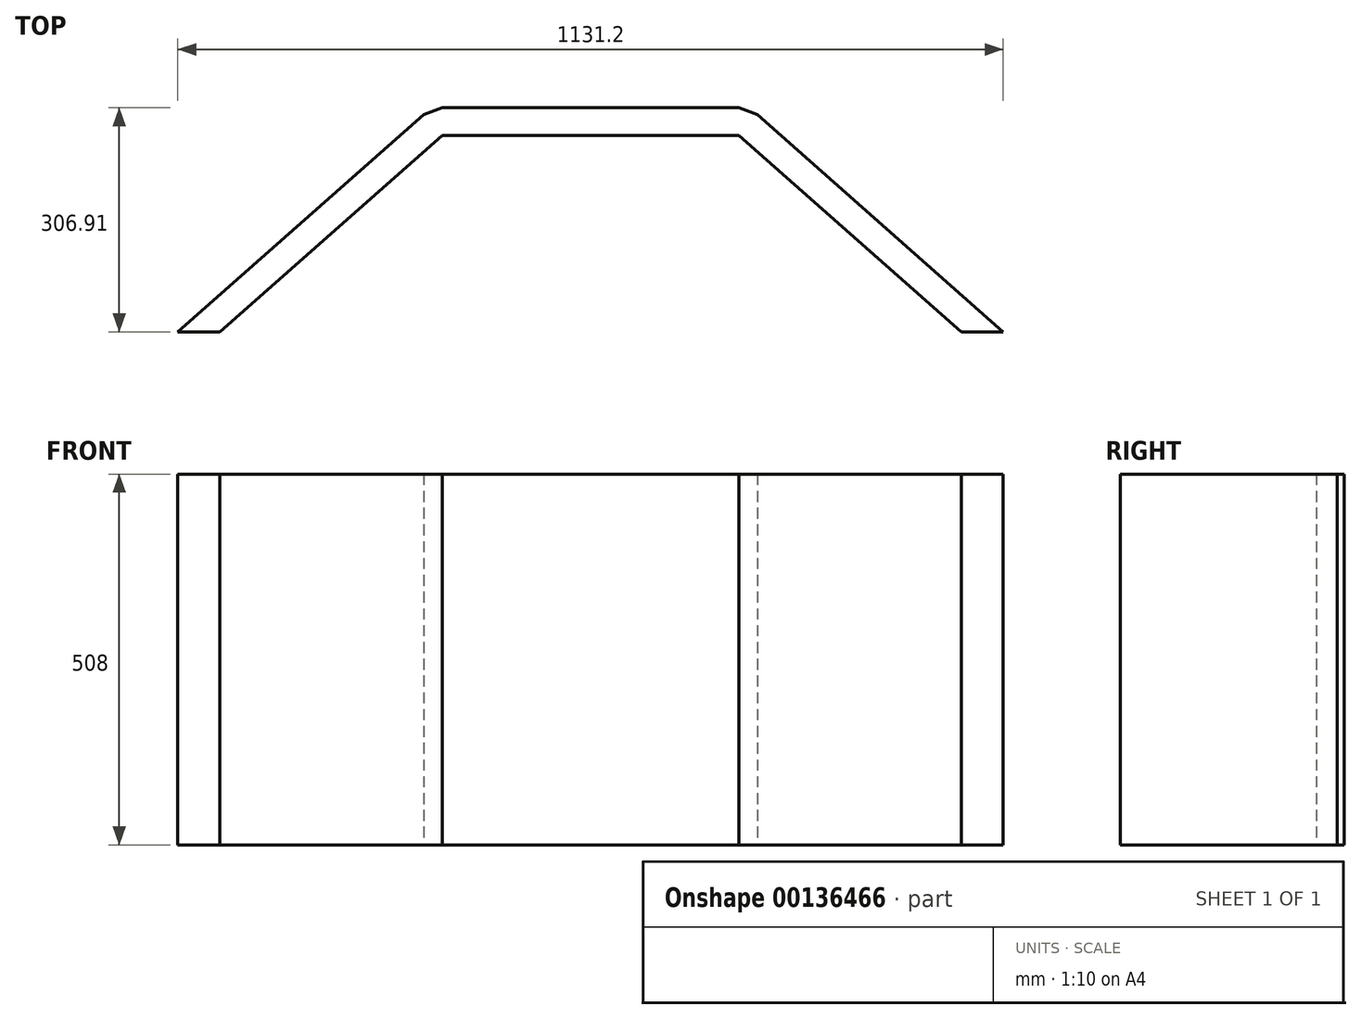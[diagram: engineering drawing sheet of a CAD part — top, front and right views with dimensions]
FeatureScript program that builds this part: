
annotation { "Feature Type Name" : "Feature", "Feature Type Description" : "" }
export const myFeature = defineFeature(function(context is Context, id is Id, definition is map)
    precondition{}
    {
        {
            var Q0;
            Q0=qCreatedBy(makeId("Top.planeOp"),FACE);
            var sketch = newSketch(context, id + "F0", { "sketchPlane" : qUnion([Q0])});
            skLineSegment(sketch, "E0", {"start": v(0, 0) * mm, "end": v(304.8, 268.8) * mm});
            skLineSegment(sketch, "E1", {"start": v(304.8, 268.8) * mm, "end": v(711.2, 268.8) * mm});
            skLineSegment(sketch, "E2", {"start": v(711.2, 268.8) * mm, "end": v(1016, 0) * mm});
            skLineSegment(sketch, "E3.top", {"start": v(304.8, 306.9) * mm, "end": v(711.2, 306.9) * mm});
            skLineSegment(sketch, "E4", {"start": v(279.6, 297.38) * mm, "end": v(-25.2, 28.58) * mm});
            skLineSegment(sketch, "E5", {"start": v(279.6, 297.38) * mm, "end": v(304.8, 306.9) * mm});
            skLineSegment(sketch, "E6", {"start": v(0, 0) * mm, "end": v(-57.6, 0) * mm});
            skLineSegment(sketch, "E7", {"start": v(-25.2, 28.57) * mm, "end": v(-57.6, 0) * mm});
            skLineSegment(sketch, "E8", {"start": v(736.4, 297.38) * mm, "end": v(1073.6, 0) * mm});
            skLineSegment(sketch, "E9", {"start": v(711.2, 306.9) * mm, "end": v(736.4, 297.38) * mm});
            skLineSegment(sketch, "E10", {"start": v(1016, 0) * mm, "end": v(1073.6, 0) * mm});
            skSolve(sketch);
        }
        {
            var Q0;
            Q0=makeQuery(id+"F0.imprint","IMPRINT",FACE,{"disambiguationData":[TD([[makeQuery(id+"F0.imprint","IMPRINT",EDGE,{"derivedFrom":sQuery(id+"F0.wireOp",EDGE,"E0")}),1.0]])]});
            extrude(context, id + "F1", {"entities" : qUnion([Q0]), "depth" : 508 * mm});
        }
    });
